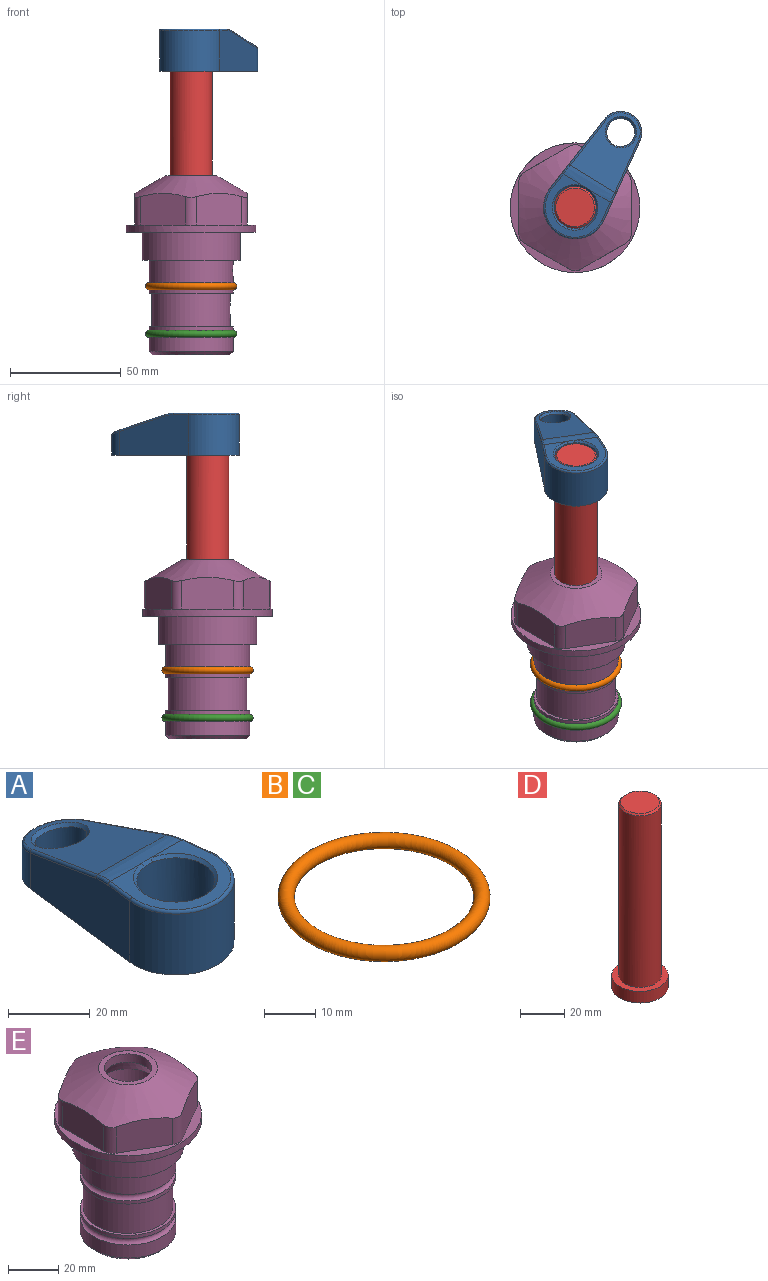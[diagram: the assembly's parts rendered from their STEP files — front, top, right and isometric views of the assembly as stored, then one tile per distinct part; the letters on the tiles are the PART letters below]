
ASSEMBLY  parts=5 mates=3
PART A: 31 faces, bbox 31.7x65.5x19.8 mm
  f0: plane 39.12x18.26mm, normal (0.99,0.12,0), area 612.2mm2, adj f1,f4,f7,f11,f13,f15
  f1: cylinder r=9.53mm len=18.91mm, axis (0,0,-1), area 296.1mm2, adj f0,f2,f7,f17
  f2: plane 39.12x18.26mm, normal (-0.99,0.12,0), area 612.2mm2, adj f1,f4,f7,f12,f14,f16
  f3: cylinder r=6.35mm len=12.7mm, axis (0,0,-1), area 362.4mm2, adj f7,f18
  f4: cylinder r=14.29mm len=28.58mm, axis (0,0,-1), area 882.2mm2, adj f0,f2,f7,f10
  f5: cylinder r=9.53mm len=19.05mm, axis (0,0,-1), area 1092.6mm2, adj f7,f19,f20
  f6: plane 26.99x23.69mm, normal (0,0,1), area 216.2mm2, adj f9,f10,f11,f12,f19
  f7: plane 63.5x28.58mm, normal (0,0,-1), area 661.8mm2, adj f0,f1,f2,f3,f4,f5,f22,f23
  f8: plane 33.52x23.6mm, normal (0,0.26,0.97), area 486mm2, adj f9,f15,f16,f17,f18
  f9: cylinder r=19.05mm len=24.72mm, axis (1,0,0), area 120.4mm2, adj f6,f8,f13,f14,f20
  f10: torus R=13.49mm, axis (0,0,1), area 59mm2, adj f4,f6,f11,f12
  f11: cylinder r=0.79mm len=8.67mm, axis (0.12,-0.99,0), area 10.8mm2, adj f0,f6,f10,f13
  f12: cylinder r=0.79mm len=8.67mm, axis (0.12,0.99,0), area 10.8mm2, adj f2,f6,f10,f14
  f13: bspline ~4.95x1.42mm, area 6.1mm2, adj f0,f9,f11,f15
  f14: bspline ~4.95x1.42mm, area 6.1mm2, adj f2,f9,f12,f16
  f15: cylinder r=0.79mm len=25.95mm, axis (0.12,-0.96,0.26), area 32.9mm2, adj f0,f8,f13,f17
  f16: cylinder r=0.79mm len=25.95mm, axis (0.12,0.96,-0.26), area 32.9mm2, adj f2,f8,f14,f17
  f17: bspline ~18.91x8.38mm, area 30mm2, adj f1,f8,f15,f16
  f18: bspline ~14.29x14.29mm, area 48.3mm2, adj f3,f8
  f19: cone r=9.53mm half-angle=45deg, axis (0,0,1), area 66.5mm2, adj f5,f6,f20
  f20: bspline ~3.22x0.96mm, area 3.5mm2, adj f5,f9,f19
  f21: plane 2.75x2.72mm, normal (0,0,-1), area 2.9mm2, adj f23,f25,f28
  f22: plane 23.05x15.88mm, normal (-0.99,-0.12,0), area 323.6mm2, adj f7,f25,f26,f27,f28,f29
  f23: plane 23.05x15.88mm, normal (0.99,-0.12,0), area 323.6mm2, adj f7,f21,f25,f27,f28,f30
  f24: cylinder r=9.53mm len=10.69mm, axis (0,0,-1), area 114.7mm2, adj f7,f27,f29,f30
  f25: cylinder r=12.7mm len=20.59mm, axis (0,0,-1), area 381.1mm2, adj f7,f21,f22,f23,f26,f28
  f26: plane 2.75x2.72mm, normal (0,0,-1), area 2.9mm2, adj f22,f25,f28
  f27: plane 19.72x18.37mm, normal (0,-0.26,-0.97), area 291.8mm2, adj f22,f23,f24,f28,f29,f30
  f28: cylinder r=15.88mm len=19.92mm, axis (1,0,0), area 54.8mm2, adj f21,f22,f23,f25,f26,f27
  f29: cylinder r=1.59mm len=11mm, axis (0,0,-1), area 34.7mm2, adj f7,f22,f24,f27
  f30: cylinder r=1.59mm len=11mm, axis (0,0,-1), area 34.7mm2, adj f7,f23,f24,f27
PART B: 1 faces, bbox 44.7x44.7x3.2 mm
  f0: torus R=19.05mm, axis (0,0,1), area 1193.9mm2
PART C: same geometry as B
PART D: 6 faces, bbox 25.4x25.4x101.6 mm
  f0: plane 17.46x17.46mm, normal (0,0,1), area 239.5mm2, adj f5
  f1: plane 25.4x25.4mm, normal (0,0,-1), area 506.7mm2, adj f2
  f2: cylinder r=12.7mm len=25.4mm, axis (0,0,1), area 506.7mm2, adj f1,f3
  f3: plane 25.4x25.4mm, normal (0,0,1), area 221.7mm2, adj f2,f4
  f4: cylinder r=9.53mm len=94.46mm, axis (0,0,1), area 5653mm2, adj f3,f5
  f5: cone r=8.73mm half-angle=45deg, axis (0,0,-1), area 64.4mm2, adj f0,f4
PART E: 36 faces, bbox 58.7x58.7x81 mm
  f0: cylinder r=17.78mm len=35.56mm, axis (0,0,1), area 1670.8mm2, adj f23,f24,f31
  f1: cylinder r=19.05mm len=38.1mm, axis (0,0,1), area 1191.9mm2, adj f26,f27,f30
  f2: plane 58.66x58.66mm, normal (0,0,-1), area 1150.6mm2, adj f3,f28
  f3: cylinder r=29.33mm len=58.66mm, axis (0,0,-1), area 585.1mm2, adj f2,f4
  f4: plane 58.66x58.66mm, normal (0,0,1), area 475.9mm2, adj f3,f5,f6,f7,f8,f9,f10,f11
  f5: plane 20.32x14.34mm, normal (-0.5,0.87,0), area 324.4mm2, adj f4,f15,f16,f17
  f6: plane 20.32x14.34mm, normal (0.5,0.87,0), area 324.4mm2, adj f4,f14,f15,f17
  f7: plane 23.48x14.34mm, normal (1,0,0), area 324.4mm2, adj f4,f13,f14,f17
  f8: plane 20.32x14.34mm, normal (0.5,-0.87,0), area 324.4mm2, adj f4,f12,f13,f17
  f9: plane 20.32x14.34mm, normal (-0.5,-0.87,0), area 324.4mm2, adj f4,f11,f12,f17
  f10: plane 23.48x14.34mm, normal (-1,0,0), area 324.4mm2, adj f4,f11,f16,f17
  f11: cylinder r=5.08mm len=12.85mm, axis (0,0,-1), area 67.2mm2, adj f4,f9,f10,f17
  f12: cylinder r=5.08mm len=12.85mm, axis (0,0,-1), area 67.2mm2, adj f4,f8,f9,f17
  f13: cylinder r=5.08mm len=12.85mm, axis (0,0,-1), area 67.2mm2, adj f4,f7,f8,f17
  f14: cylinder r=5.08mm len=12.85mm, axis (0,0,-1), area 67.2mm2, adj f4,f6,f7,f17
  f15: cylinder r=5.08mm len=12.85mm, axis (0,0,-1), area 67.2mm2, adj f4,f5,f6,f17
  f16: cylinder r=5.08mm len=12.85mm, axis (0,0,-1), area 67.2mm2, adj f4,f5,f10,f17
  f17: cone r=11.73mm half-angle=60deg, axis (0,0,-1), area 2071.8mm2, adj f5,f6,f7,f8,f9,f10,f11,f12
  f18: plane 23.46x23.46mm, normal (0,0,1), area 147.4mm2, adj f17,f35
  f19: plane 34.93x34.93mm, normal (0,0,-1), area 958mm2, adj f29
  f20: cylinder r=19.05mm len=38.1mm, axis (0,0,1), area 760.1mm2, adj f21,f29
  f21: torus R=19.05mm, axis (0,0,1), area 565.3mm2, adj f20,f22
  f22: cylinder r=19.05mm len=38.1mm, axis (0,0,1), area 190mm2, adj f21,f23
  f23: plane 38.1x38.1mm, normal (0,0,1), area 146.9mm2, adj f0,f22
  f24: plane 38.1x38.1mm, normal (0,0,-1), area 146.9mm2, adj f0,f25
  f25: cylinder r=19.05mm len=38.1mm, axis (0,0,1), area 190mm2, adj f24,f26
  f26: torus R=19.05mm, axis (0,0,1), area 565.3mm2, adj f1,f25
  f27: plane 44.45x44.45mm, normal (0,0,-1), area 411.7mm2, adj f1,f28
  f28: cylinder r=22.23mm len=44.45mm, axis (0,0,1), area 1773.5mm2, adj f2,f27
  f29: cone r=19.05mm half-angle=45deg, axis (0,0,1), area 257.5mm2, adj f19,f20
  f30: cylinder r=3.17mm len=6.75mm, axis (-1,0,0), area 128mm2, adj f1,f33
  f31: cylinder r=3.17mm len=6.35mm, axis (-1,0,0), area 102.5mm2, adj f0,f33
  f32: plane 25.4x25.4mm, normal (0,0,1), area 506.7mm2, adj f33
  f33: cylinder r=12.7mm len=66.42mm, axis (0,0,-1), area 5236.2mm2, adj f30,f31,f32,f34
  f34: cone r=9.53mm half-angle=30deg, axis (0,0,-1), area 443.4mm2, adj f33,f35
  f35: cylinder r=9.53mm len=19.05mm, axis (0,0,-1), area 240.9mm2, adj f18,f34
PLACE A rot(axis=(0,0,-1),31.3deg) t=(0,0,28.35)mm
PLACE B at identity
PLACE C t=(0,0,-21.59)mm
PLACE D rot(axis=(0,0,-1),31.3deg) t=(0,0,27.55)mm
PLACE E at identity fixed
MATE cylindrical D.f2 <-> E.f0  axis (0,0,-1) through (0,0,-10.55)mm
MATE fastened C.f0 <-> E.f0  axis (0,0,1) through (0,0,-46.1)mm
MATE fastened A.f4 <-> D.f2  axis (0,0,1) through (0,0,91.05)mm
